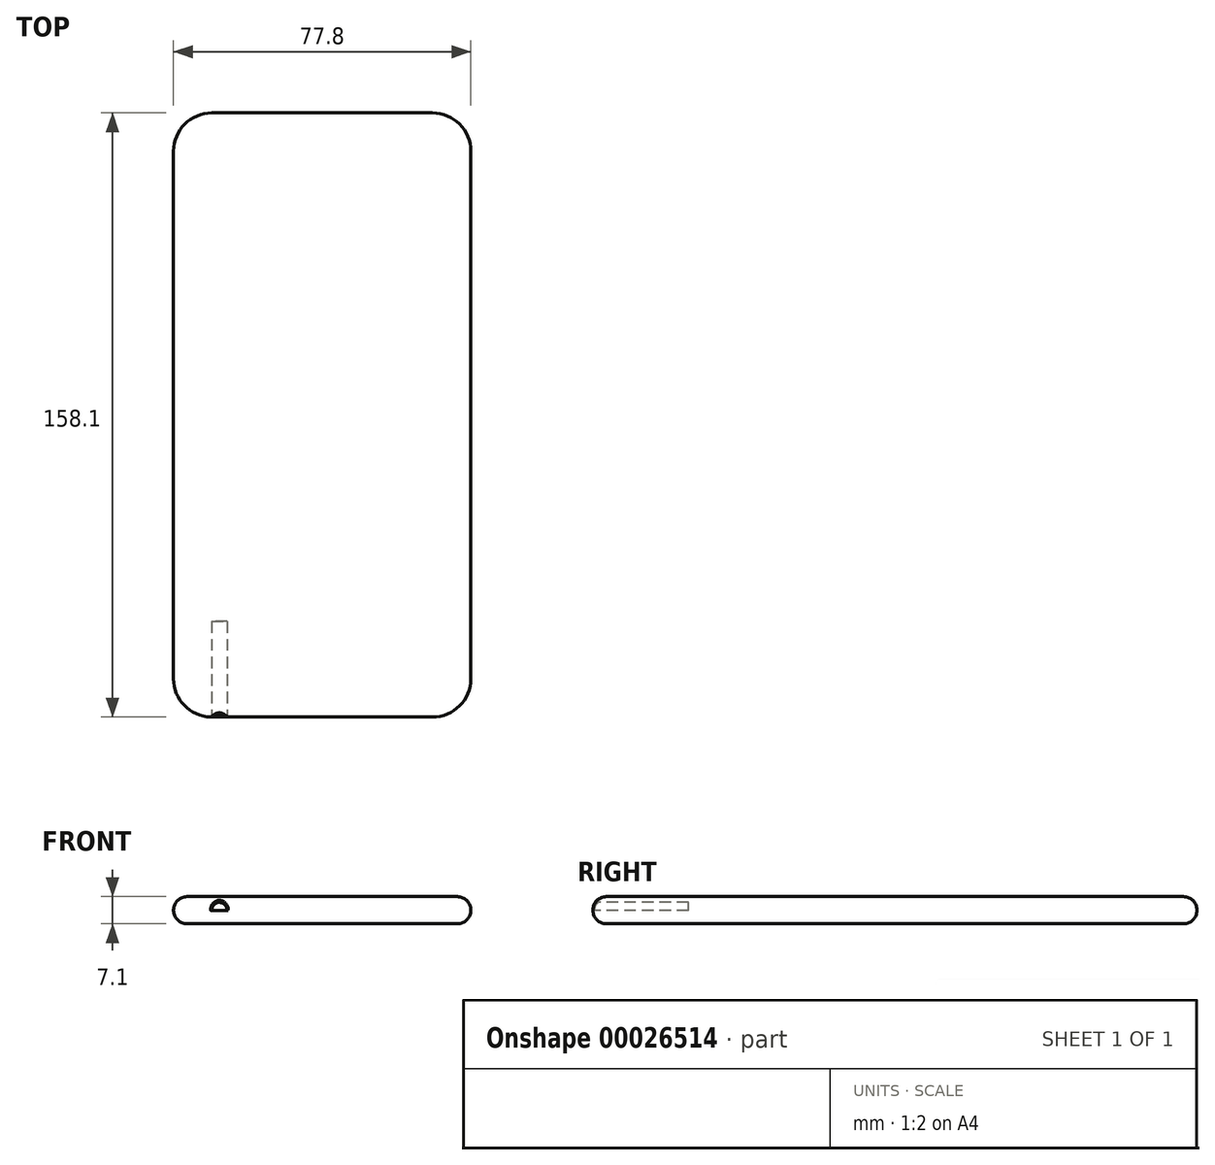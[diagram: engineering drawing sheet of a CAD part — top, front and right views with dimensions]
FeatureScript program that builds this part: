
annotation { "Feature Type Name" : "Feature", "Feature Type Description" : "" }
export const myFeature = defineFeature(function(context is Context, id is Id, definition is map)
    precondition{}
    {
        {
            var Q0;
            Q0=qCreatedBy(makeId("Top.planeOp"),FACE);
            var sketch = newSketch(context, id + "F0", { "sketchPlane" : qUnion([Q0])});
            skLineSegment(sketch, "E0.bottom", {"start": v(-47.98, 74.37) * mm, "end": v(29.82, 74.37) * mm});
            skLineSegment(sketch, "E0.top", {"start": v(-47.98, -83.73) * mm, "end": v(29.82, -83.73) * mm});
            skLineSegment(sketch, "E0.left", {"start": v(-47.98, 74.37) * mm, "end": v(-47.98, -83.73) * mm});
            skLineSegment(sketch, "E0.right", {"start": v(29.82, 74.37) * mm, "end": v(29.82, -83.73) * mm});
            skSolve(sketch);
        }
        {
            var Q0;
            Q0=makeQuery(id+"F0.imprint","IMPRINT",FACE,{"disambiguationData":[TD([[makeQuery(id+"F0.imprint","IMPRINT",EDGE,{"derivedFrom":sQuery(id+"F0.wireOp",EDGE,"E0.bottom")}),-1.0]])]});
            extrude(context, id + "F1", {"entities" : qUnion([Q0]), "depth" : 7.1 * mm});
        }
        {
            var Q0;
            Q0=makeQuery(id+"F1.opExtrude","SWEPT_EDGE",EDGE,{"disambiguationData":[OSD([sQuery(id+"F0.wireOp",EDGE,"E0.top"),sQuery(id+"F0.wireOp",EDGE,"E0.right")])]});
            var Q1;
            Q1=makeQuery(id+"F1.opExtrude","SWEPT_EDGE",EDGE,{"disambiguationData":[OSD([sQuery(id+"F0.wireOp",EDGE,"E0.top"),sQuery(id+"F0.wireOp",EDGE,"E0.left")])]});
            var Q2;
            Q2=makeQuery(id+"F1.opExtrude","SWEPT_EDGE",EDGE,{"disambiguationData":[OSD([sQuery(id+"F0.wireOp",EDGE,"E0.bottom"),sQuery(id+"F0.wireOp",EDGE,"E0.right")])]});
            var Q3;
            Q3=makeQuery(id+"F1.opExtrude","SWEPT_EDGE",EDGE,{"disambiguationData":[OSD([sQuery(id+"F0.wireOp",EDGE,"E0.bottom"),sQuery(id+"F0.wireOp",EDGE,"E0.left")])]});
            fillet(context, id + "F2", {"entities" : qUnion([Q0, Q1, Q2, Q3]), "radius" : 10 * mm, "tangentPropagation" : true, "allowEdgeOverflow" : false});
        }
        {
            var Q0;
            Q0=makeQuery(id+"F1.opExtrude","CAP_FACE",FACE,{"disambiguationData":[OSD([sQuery(id+"F0.wireOp",EDGE,"E0.bottom"),sQuery(id+"F0.wireOp",EDGE,"E0.top"),sQuery(id+"F0.wireOp",EDGE,"E0.left"),sQuery(id+"F0.wireOp",EDGE,"E0.right")])],"isStart":false});
            var Q1;
            Q1=makeQuery(id+"F1.opExtrude","CAP_FACE",FACE,{"disambiguationData":[OSD([sQuery(id+"F0.wireOp",EDGE,"E0.bottom"),sQuery(id+"F0.wireOp",EDGE,"E0.top"),sQuery(id+"F0.wireOp",EDGE,"E0.left"),sQuery(id+"F0.wireOp",EDGE,"E0.right")])],"isStart":true});
            fillet(context, id + "F3", {"entities" : qUnion([Q0, Q1]), "radius" : 3.5 * mm, "tangentPropagation" : true, "allowEdgeOverflow" : false});
        }
        {
            var Q0;
            Q0=makeQuery(id+"F1.opExtrude","SWEPT_FACE",FACE,{"disambiguationData":[OSD([sQuery(id+"F0.wireOp",EDGE,"E0.top")])]});
            var sketch = newSketch(context, id + "F4", { "sketchPlane" : qUnion([Q0])});
            skCircle(sketch, "E1", {"center": v(-35.98, 3.6) * mm, "radius": 2 * mm});
            skSolve(sketch);
        }
        {
            var Q0;
            {var subQ0=sQuery(id+"F0.wireOp",EDGE,"E0.top");var subQ1=makeQuery(id+"F1.opExtrude","SWEPT_FACE",FACE,{"disambiguationData":[OSD([subQ0])]});var subQ2=makeQuery(id+"F3.opFillet","BLEND_EDGE",EDGE,{"blendedFrom":[makeQuery(id+"F1.opExtrude","CAP_EDGE",EDGE,{"disambiguationData":[OSD([subQ0])],"isStart":false}),subQ1],"blendedInto":[subQ1]});var subQ3=sQuery(id+"F4.wireOp",EDGE,"E1");var subQ4=makeQuery(id+"F4.imprint","INTERSECT",VERTEX,{"derivedFrom":[subQ2,subQ3]});Q0=makeQuery(id+"F4.imprint","IMPRINT",FACE,{"disambiguationData":[TD([[makeQuery(id+"F4.imprint","IMPRINT",EDGE,{"disambiguationData":[TD([[subQ4,-1.0]])],"derivedFrom":subQ3}),1.0]])]});}
            var Q1;
            {var subQ0=sQuery(id+"F0.wireOp",EDGE,"E0.top");var subQ1=makeQuery(id+"F3.opFillet","BLEND_EDGE",EDGE,{"blendedFrom":[makeQuery(id+"F1.opExtrude","CAP_EDGE",EDGE,{"disambiguationData":[OSD([subQ0])],"isStart":true}),makeQuery(id+"F1.opExtrude","SWEPT_FACE",FACE,{"disambiguationData":[OSD([subQ0])]})],"blendedInto":[makeQuery(id+"F1.opExtrude","SWEPT_FACE",FACE,{"disambiguationData":[OSD([subQ0])]})]});var subQ2=sQuery(id+"F4.wireOp",EDGE,"E1");var subQ4=makeQuery(id+"F4.imprint","INTERSECT",VERTEX,{"disambiguationData":[OD(0.0)],"derivedFrom":[subQ1,subQ2]});Q1=makeQuery(id+"F4.imprint","IMPRINT",FACE,{"disambiguationData":[TD([[makeQuery(id+"F4.imprint","IMPRINT",EDGE,{"disambiguationData":[TD([[subQ4,-1.0]])],"derivedFrom":subQ2}),1.0]])]});}
            var Q2;
            {var subQ0=sQuery(id+"F0.wireOp",EDGE,"E0.top");var subQ1=makeQuery(id+"F1.opExtrude","SWEPT_FACE",FACE,{"disambiguationData":[OSD([subQ0])]});var subQ2=subQ1;var subQ3=makeQuery(id+"F3.opFillet","BLEND_EDGE",EDGE,{"blendedFrom":[makeQuery(id+"F1.opExtrude","CAP_EDGE",EDGE,{"disambiguationData":[OSD([subQ0])],"isStart":false}),subQ2],"blendedInto":[subQ2]});var subQ4=sQuery(id+"F4.wireOp",EDGE,"E1");var subQ5=makeQuery(id+"F4.imprint","INTERSECT",VERTEX,{"derivedFrom":[subQ3,subQ4]});Q2=makeQuery(id+"F4.imprint","IMPRINT",FACE,{"disambiguationData":[TD([[makeQuery(id+"F4.imprint","IMPRINT",EDGE,{"disambiguationData":[TD([[subQ5,1.0]])],"derivedFrom":subQ4}),1.0]])]});}
            extrude(context, id + "F5", {"entities" : qUnion([Q0, Q1, Q2]), "operationType" : NewBodyOperationType.REMOVE, "oppositeDirection" : true, "depth" : 25 * mm});
        }
        {
            var Q0;
            {var subQ0=sQuery(id+"F0.wireOp",EDGE,"E0.top");Q0=makeQuery(id+"F5.boolean.opBoolean","INTERSECT",EDGE,{"derivedFrom":[makeQuery(id+"F3.opFillet","BLEND_FACE",FACE,{"disambiguationData":[OSD([subQ0]),TDD([makeQuery(id+"F1.opExtrude","CAP_EDGE",EDGE,{"disambiguationData":[OSD([subQ0])],"isStart":false})])]}),makeQuery(id+"F5.opExtrude","SWEPT_FACE",FACE,{"disambiguationData":[OSD([sQuery(id+"F4.wireOp",EDGE,"E1")])]})]});}
            var Q1;
            {var subQ0=sQuery(id+"F0.wireOp",EDGE,"E0.top");Q1=makeQuery(id+"F5.boolean.opBoolean","INTERSECT",EDGE,{"derivedFrom":[makeQuery(id+"F3.opFillet","BLEND_FACE",FACE,{"disambiguationData":[OSD([subQ0]),TDD([makeQuery(id+"F1.opExtrude","CAP_EDGE",EDGE,{"disambiguationData":[OSD([subQ0])],"isStart":true})])]}),makeQuery(id+"F5.opExtrude","SWEPT_FACE",FACE,{"disambiguationData":[OSD([sQuery(id+"F4.wireOp",EDGE,"E1")])]})]});}
            var Q2;
            Q2=makeQuery(id+"F5.boolean.opBoolean","COPY",EDGE,{"disambiguationData":[OD(0.0)],"derivedFrom":makeQuery(id+"F5.opExtrude","CAP_EDGE",EDGE,{"disambiguationData":[OSD([sQuery(id+"F4.wireOp",EDGE,"E1")])],"isStart":true})});
            var Q3;
            Q3=makeQuery(id+"F5.boolean.opBoolean","COPY",EDGE,{"disambiguationData":[OD(1.0)],"derivedFrom":makeQuery(id+"F5.opExtrude","CAP_EDGE",EDGE,{"disambiguationData":[OSD([sQuery(id+"F4.wireOp",EDGE,"E1")])],"isStart":true})});
            fillet(context, id + "F6", {"entities" : qUnion([Q0, Q1, Q2, Q3]), "radius" : 0.3 * mm, "tangentPropagation" : true, "allowEdgeOverflow" : false});
        }
    });
